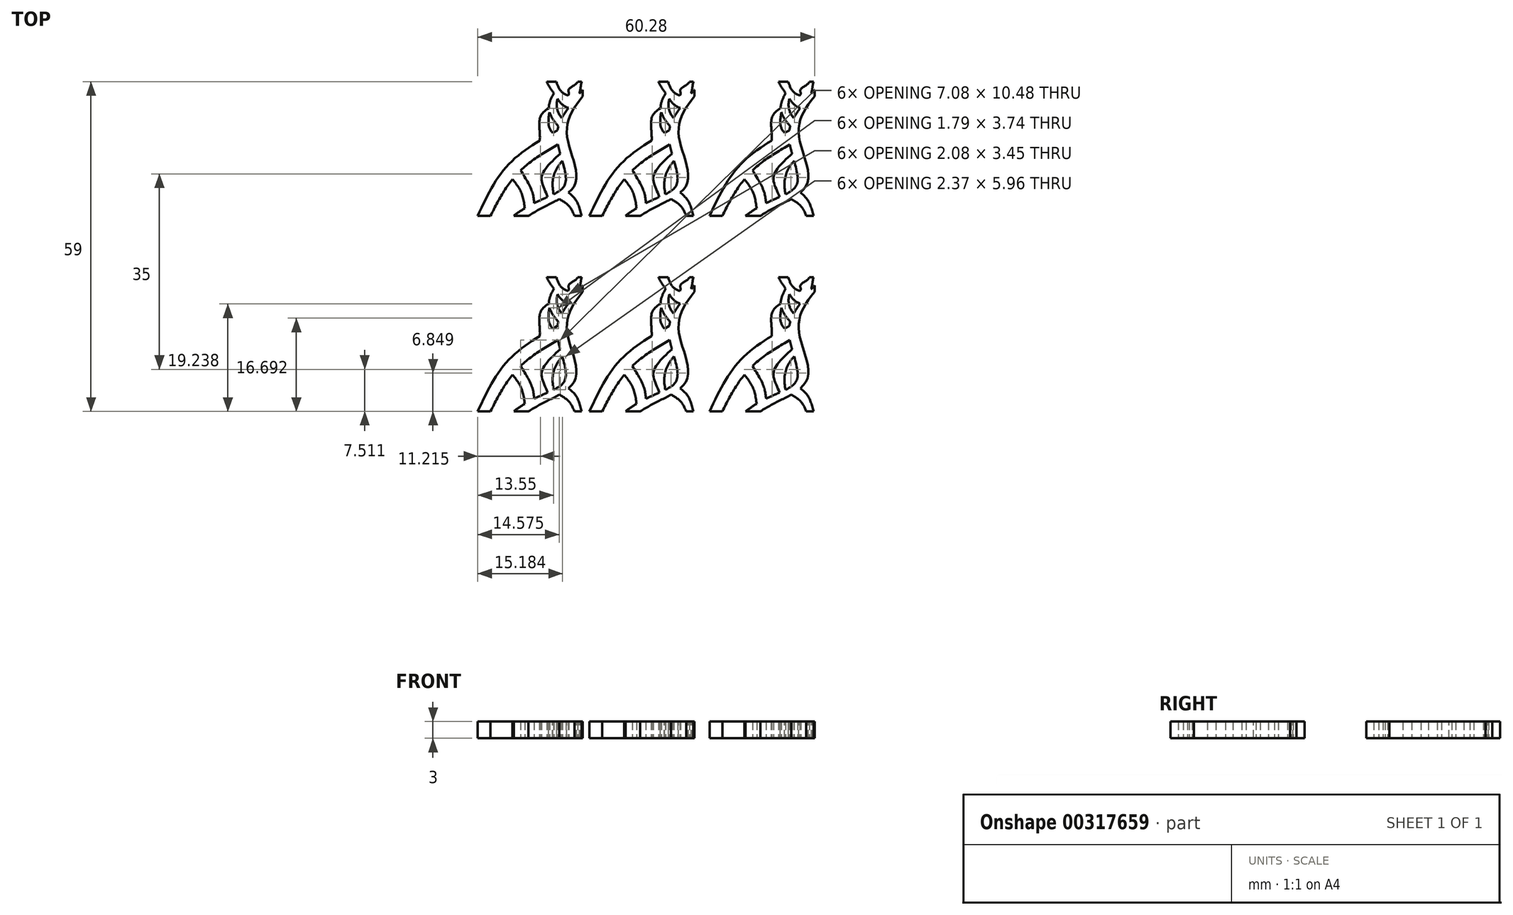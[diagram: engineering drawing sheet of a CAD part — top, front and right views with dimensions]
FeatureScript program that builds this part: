
annotation { "Feature Type Name" : "Feature", "Feature Type Description" : "" }
export const myFeature = defineFeature(function(context is Context, id is Id, definition is map)
    precondition{}
    {
        {
            var Q0;
            Q0=qCreatedBy(makeId("Top.planeOp"),FACE);
            var sketch = newSketch(context, id + "F0", { "sketchPlane" : qUnion([Q0])});
            skLineSegment(sketch, "E0.bottom", {"start": v(161.57, 207.7) * mm, "end": v(-151.57, 207.7) * mm});
            skLineSegment(sketch, "E0.top", {"start": v(161.57, -192.3) * mm, "end": v(-151.57, -192.3) * mm});
            skLineSegment(sketch, "E0.left", {"start": v(161.57, 207.7) * mm, "end": v(161.57, -192.3) * mm});
            skLineSegment(sketch, "E0.right", {"start": v(-151.57, 207.7) * mm, "end": v(-151.57, -192.3) * mm});
            skFitSpline(sketch, "E1", {"points": [v(161.57, 183.5) * mm, v(85.12, 44.75) * mm, v(109.31, -96.4) * mm, v(-44.12, -192.3) * mm], "startDerivative": vector(-382, -492.17) * mm, "endDerivative": vector(-632.26, -490) * mm});
            skFitSpline(sketch, "E2", {"points": [v(161.57, 164.23) * mm, v(115.12, 45.06) * mm, v(139.33, -96.46) * mm, v(0, -192.3) * mm], "startDerivative": vector(-323.93, -389.82) * mm, "endDerivative": vector(-432.8, -289.86) * mm});
            skFitSpline(sketch, "E3", {"points": [v(87.95, 20.15) * mm, v(-36.08, -69.46) * mm, v(-113.36, -192.3) * mm], "startDerivative": vector(-287.2, -159.14) * mm, "endDerivative": vector(-134.26, -271.05) * mm});
            skFitSpline(sketch, "E4", {"points": [v(86.4, 62.77) * mm, v(-60.96, -40.6) * mm, v(-151.57, -192.3) * mm], "startDerivative": vector(-322.1, -181.09) * mm, "endDerivative": vector(-154.33, -329.73) * mm});
            skFitSpline(sketch, "E5", {"points": [v(91.66, -142.16) * mm, v(120.33, -162.57) * mm, v(137.1, -192.3) * mm], "startDerivative": vector(63.12, -36.39) * mm, "endDerivative": vector(28.09, -64.9) * mm});
            skFitSpline(sketch, "E6", {"points": [v(119.32, -123.08) * mm, v(142.68, -147.67) * mm, v(158.5, -192.3) * mm], "startDerivative": vector(55.7, -46.78) * mm, "endDerivative": vector(23.32, -90.23) * mm});
            skFitSpline(sketch, "E7", {"points": [v(100.65, -28.51) * mm, v(73.78, -78.77) * mm, v(75.03, -127.85) * mm], "startDerivative": vector(-88.91, -98.41) * mm, "endDerivative": vector(24.95, -113.83) * mm});
            skFitSpline(sketch, "E8", {"points": [v(94.41, -6.72) * mm, v(39.45, -75.98) * mm, v(57.07, -136.12) * mm], "startDerivative": vector(-135.48, -128.88) * mm, "endDerivative": vector(50.2, -141.27) * mm});
            skFitSpline(sketch, "E9", {"points": [v(54.23, 207.7) * mm, v(81.23, 165.16) * mm, v(119.4, 129.17) * mm], "startDerivative": vector(44.56, -99.42) * mm, "endDerivative": vector(118.17, -31.75) * mm});
            skFitSpline(sketch, "E10", {"points": [v(83.1, 207.7) * mm, v(99.85, 176.33) * mm, v(142.84, 159.86) * mm], "startDerivative": vector(25.78, -76.02) * mm, "endDerivative": vector(99.84, -29.98) * mm});
            skFitSpline(sketch, "E11", {"points": [v(146.4, 207.7) * mm, v(119.4, 183.78) * mm, v(118, 167.02) * mm], "startDerivative": vector(-16.59, -50.41) * mm, "endDerivative": vector(-40.58, -34) * mm});
            skFitSpline(sketch, "E12", {"points": [v(158.5, 207.7) * mm, v(153.85, 181.92) * mm, v(152.97, 172.55) * mm], "startDerivative": vector(-12.64, -48.27) * mm, "endDerivative": vector(10.98, -30.7) * mm});
            skFitSpline(sketch, "E13", {"points": [v(75.43, 173.52) * mm, v(60.75, 128.85) * mm, v(89.2, 75) * mm], "startDerivative": vector(-54.24, -96.72) * mm, "endDerivative": vector(96.14, -103.87) * mm});
            skFitSpline(sketch, "E14", {"points": [v(86.56, 157.05) * mm, v(84.95, 128.85) * mm, v(99.53, 99.55) * mm], "startDerivative": vector(-16.02, -62.32) * mm, "endDerivative": vector(51.54, -60.1) * mm});
            skFitSpline(sketch, "E15", {"points": [v(62.75, 117) * mm, v(60.75, 74.85) * mm, v(72.13, 54.72) * mm], "startDerivative": vector(-16.42, -83.23) * mm, "endDerivative": vector(39.32, -49.75) * mm});
            skFitSpline(sketch, "E16", {"points": [v(60.75, 128.85) * mm, v(35.6, 103.71) * mm, v(32.47, 71.12) * mm, v(33.8, 32.44) * mm], "startDerivative": vector(-112.87, -59.98) * mm, "endDerivative": vector(-6.89, -98.92) * mm});
            skFitSpline(sketch, "E17", {"points": [v(-47.68, -82.88) * mm, v(-21.54, -123.28) * mm, v(-11.06, -169.71) * mm], "startDerivative": vector(59.74, -77.34) * mm, "endDerivative": vector(13.37, -96.33) * mm});
            skFitSpline(sketch, "E18", {"points": [v(-23.58, -56.72) * mm, v(10.06, -118.02) * mm, v(16.93, -154.44) * mm], "startDerivative": vector(70.14, -111.5) * mm, "endDerivative": vector(7.52, -82.35) * mm});
            skSolve(sketch);
        }
        {
            var Q0;
            {var subQ0=sQuery(id+"F0.wireOp",EDGE,"E3");var subQ3=sQuery(id+"F0.wireOp",EDGE,"E1");var subQ4=makeQuery(id+"F0.imprint","INTERSECT",VERTEX,{"derivedFrom":[subQ3,subQ0]});Q0=makeQuery(id+"F0.imprint","IMPRINT",FACE,{"disambiguationData":[TD([[makeQuery(id+"F0.imprint","IMPRINT",EDGE,{"disambiguationData":[TD([[subQ4,1.0]])],"derivedFrom":subQ3}),-1.0]])]});}
            var Q1;
            {var subQ0=sQuery(id+"F0.wireOp",EDGE,"E17");Q1=makeQuery(id+"F0.imprint","IMPRINT",FACE,{"disambiguationData":[TD([[makeQuery(id+"F0.imprint","IMPRINT",EDGE,{"derivedFrom":subQ0}),1.0]])]});}
            var Q2;
            {var subQ0=sQuery(id+"F0.wireOp",EDGE,"E1");var subQ9=sQuery(id+"F0.wireOp",EDGE,"E0.top");var subQ10=makeQuery(id+"F0.imprint","INTERSECT",VERTEX,{"derivedFrom":[subQ9,subQ0]});Q2=makeQuery(id+"F0.imprint","IMPRINT",FACE,{"disambiguationData":[TD([[makeQuery(id+"F0.imprint","IMPRINT",EDGE,{"disambiguationData":[TD([[subQ10,1.0]])],"derivedFrom":subQ9}),-1.0]])]});}
            var Q3;
            {var subQ0=sQuery(id+"F0.wireOp",EDGE,"E5");Q3=makeQuery(id+"F0.imprint","IMPRINT",FACE,{"disambiguationData":[TD([[makeQuery(id+"F0.imprint","IMPRINT",EDGE,{"derivedFrom":subQ0}),1.0]])]});}
            var Q4;
            {var subQ0=sQuery(id+"F0.wireOp",EDGE,"E7");Q4=makeQuery(id+"F0.imprint","IMPRINT",FACE,{"disambiguationData":[TD([[makeQuery(id+"F0.imprint","IMPRINT",EDGE,{"derivedFrom":subQ0}),-1.0]])]});}
            var Q5;
            {var subQ0=sQuery(id+"F0.wireOp",EDGE,"E15");Q5=makeQuery(id+"F0.imprint","IMPRINT",FACE,{"disambiguationData":[TD([[makeQuery(id+"F0.imprint","IMPRINT",EDGE,{"derivedFrom":subQ0}),-1.0]])]});}
            var Q6;
            {var subQ5=sQuery(id+"F0.wireOp",EDGE,"E14");Q6=makeQuery(id+"F0.imprint","IMPRINT",FACE,{"disambiguationData":[TD([[makeQuery(id+"F0.imprint","IMPRINT",EDGE,{"derivedFrom":subQ5}),-1.0]])]});}
            var Q7;
            {var subQ0=sQuery(id+"F0.wireOp",EDGE,"E9");var subQ1=sQuery(id+"F0.wireOp",EDGE,"E0.bottom");var subQ2=makeQuery(id+"F0.imprint","INTERSECT",VERTEX,{"derivedFrom":[subQ1,subQ0]});Q7=makeQuery(id+"F0.imprint","IMPRINT",FACE,{"disambiguationData":[TD([[makeQuery(id+"F0.imprint","IMPRINT",EDGE,{"disambiguationData":[TD([[subQ2,1.0]])],"derivedFrom":subQ1}),1.0]])]});}
            var Q8;
            {var subQ0=sQuery(id+"F0.wireOp",EDGE,"E11");Q8=makeQuery(id+"F0.imprint","IMPRINT",FACE,{"disambiguationData":[TD([[makeQuery(id+"F0.imprint","IMPRINT",EDGE,{"derivedFrom":subQ0}),1.0]])]});}
            extrude(context, id + "F1", {"entities" : qUnion([Q0, Q1, Q2, Q3, Q4, Q5, Q6, Q7, Q8]), "depth" : 50 * mm});
        }
        {
            var Q0;
            Q0=makeQuery(id+"F1.opExtrude","SWEPT_BODY",BODY,{"disambiguationData":[OSD([sQuery(id+"F0.wireOp",EDGE,"E0.bottom"),sQuery(id+"F0.wireOp",EDGE,"E0.top"),sQuery(id+"F0.wireOp",EDGE,"E0.left"),sQuery(id+"F0.wireOp",EDGE,"E1"),sQuery(id+"F0.wireOp",EDGE,"E2"),sQuery(id+"F0.wireOp",EDGE,"E3"),sQuery(id+"F0.wireOp",EDGE,"E4"),sQuery(id+"F0.wireOp",EDGE,"E5"),sQuery(id+"F0.wireOp",EDGE,"E6"),sQuery(id+"F0.wireOp",EDGE,"E7"),sQuery(id+"F0.wireOp",EDGE,"E8"),sQuery(id+"F0.wireOp",EDGE,"E9"),sQuery(id+"F0.wireOp",EDGE,"E10"),sQuery(id+"F0.wireOp",EDGE,"E11"),sQuery(id+"F0.wireOp",EDGE,"E12"),sQuery(id+"F0.wireOp",EDGE,"E13"),sQuery(id+"F0.wireOp",EDGE,"E14"),sQuery(id+"F0.wireOp",EDGE,"E15"),sQuery(id+"F0.wireOp",EDGE,"E16"),sQuery(id+"F0.wireOp",EDGE,"E17"),sQuery(id+"F0.wireOp",EDGE,"E18")])]});
            var Q1;
            Q1=qCreatedBy(makeId("Origin.pointOp"),VERTEX);
            var Q2;
            Q2=qCreatedBy(makeId("Origin.pointOp"),VERTEX);
            transform(context, id + "F2", {"entities" : qUnion([Q0]), "transformType" : TransformType.SCALE_UNIFORMLY, "scale" : 0.06, "scalePoint" : qUnion([Q2]), "makeCopy" : false});
        }
        {
            var Q0;
            Q0=makeQuery(id+"F1.opExtrude","SWEPT_BODY",BODY,{"disambiguationData":[OSD([sQuery(id+"F0.wireOp",EDGE,"E0.bottom"),sQuery(id+"F0.wireOp",EDGE,"E0.top"),sQuery(id+"F0.wireOp",EDGE,"E0.left"),sQuery(id+"F0.wireOp",EDGE,"E1"),sQuery(id+"F0.wireOp",EDGE,"E2"),sQuery(id+"F0.wireOp",EDGE,"E3"),sQuery(id+"F0.wireOp",EDGE,"E4"),sQuery(id+"F0.wireOp",EDGE,"E5"),sQuery(id+"F0.wireOp",EDGE,"E6"),sQuery(id+"F0.wireOp",EDGE,"E7"),sQuery(id+"F0.wireOp",EDGE,"E8"),sQuery(id+"F0.wireOp",EDGE,"E9"),sQuery(id+"F0.wireOp",EDGE,"E10"),sQuery(id+"F0.wireOp",EDGE,"E11"),sQuery(id+"F0.wireOp",EDGE,"E12"),sQuery(id+"F0.wireOp",EDGE,"E13"),sQuery(id+"F0.wireOp",EDGE,"E14"),sQuery(id+"F0.wireOp",EDGE,"E15"),sQuery(id+"F0.wireOp",EDGE,"E16"),sQuery(id+"F0.wireOp",EDGE,"E17"),sQuery(id+"F0.wireOp",EDGE,"E18")])]});
            transform(context, id + "F3", {"entities" : qUnion([Q0]), "transformType" : TransformType.TRANSLATION_3D, "dx" : 21.5 * mm, "dy" : 0 * mm, "dz" : 0 * mm, "makeCopy" : true});
        }
        {
            var Q0;
            Q0=makeQuery(id+"F1.opExtrude","SWEPT_BODY",BODY,{"disambiguationData":[OSD([sQuery(id+"F0.wireOp",EDGE,"E0.bottom"),sQuery(id+"F0.wireOp",EDGE,"E0.top"),sQuery(id+"F0.wireOp",EDGE,"E0.left"),sQuery(id+"F0.wireOp",EDGE,"E1"),sQuery(id+"F0.wireOp",EDGE,"E2"),sQuery(id+"F0.wireOp",EDGE,"E3"),sQuery(id+"F0.wireOp",EDGE,"E4"),sQuery(id+"F0.wireOp",EDGE,"E5"),sQuery(id+"F0.wireOp",EDGE,"E6"),sQuery(id+"F0.wireOp",EDGE,"E7"),sQuery(id+"F0.wireOp",EDGE,"E8"),sQuery(id+"F0.wireOp",EDGE,"E9"),sQuery(id+"F0.wireOp",EDGE,"E10"),sQuery(id+"F0.wireOp",EDGE,"E11"),sQuery(id+"F0.wireOp",EDGE,"E12"),sQuery(id+"F0.wireOp",EDGE,"E13"),sQuery(id+"F0.wireOp",EDGE,"E14"),sQuery(id+"F0.wireOp",EDGE,"E15"),sQuery(id+"F0.wireOp",EDGE,"E16"),sQuery(id+"F0.wireOp",EDGE,"E17"),sQuery(id+"F0.wireOp",EDGE,"E18")])]});
            transform(context, id + "F4", {"entities" : qUnion([Q0]), "transformType" : TransformType.TRANSLATION_3D, "dx" : -20 * mm, "dy" : 0 * mm, "dz" : 0 * mm, "makeCopy" : true});
        }
        {
            var Q0;
            Q0=makeQuery(id+"F1.opExtrude","SWEPT_BODY",BODY,{"disambiguationData":[OSD([sQuery(id+"F0.wireOp",EDGE,"E0.bottom"),sQuery(id+"F0.wireOp",EDGE,"E0.top"),sQuery(id+"F0.wireOp",EDGE,"E0.left"),sQuery(id+"F0.wireOp",EDGE,"E1"),sQuery(id+"F0.wireOp",EDGE,"E2"),sQuery(id+"F0.wireOp",EDGE,"E3"),sQuery(id+"F0.wireOp",EDGE,"E4"),sQuery(id+"F0.wireOp",EDGE,"E5"),sQuery(id+"F0.wireOp",EDGE,"E6"),sQuery(id+"F0.wireOp",EDGE,"E7"),sQuery(id+"F0.wireOp",EDGE,"E8"),sQuery(id+"F0.wireOp",EDGE,"E9"),sQuery(id+"F0.wireOp",EDGE,"E10"),sQuery(id+"F0.wireOp",EDGE,"E11"),sQuery(id+"F0.wireOp",EDGE,"E12"),sQuery(id+"F0.wireOp",EDGE,"E13"),sQuery(id+"F0.wireOp",EDGE,"E14"),sQuery(id+"F0.wireOp",EDGE,"E15"),sQuery(id+"F0.wireOp",EDGE,"E16"),sQuery(id+"F0.wireOp",EDGE,"E17"),sQuery(id+"F0.wireOp",EDGE,"E18")])]});
            transform(context, id + "F5", {"entities" : qUnion([Q0]), "transformType" : TransformType.TRANSLATION_3D, "dx" : 0 * mm, "dy" : 35 * mm, "dz" : 0 * mm, "makeCopy" : true});
        }
        {
            var Q0;
            Q0=makeQuery(id+"F3.opPattern","COPY",BODY,{"derivedFrom":makeQuery(id+"F1.opExtrude","SWEPT_BODY",BODY,{"disambiguationData":[OSD([sQuery(id+"F0.wireOp",EDGE,"E0.bottom"),sQuery(id+"F0.wireOp",EDGE,"E0.top"),sQuery(id+"F0.wireOp",EDGE,"E0.left"),sQuery(id+"F0.wireOp",EDGE,"E1"),sQuery(id+"F0.wireOp",EDGE,"E2"),sQuery(id+"F0.wireOp",EDGE,"E3"),sQuery(id+"F0.wireOp",EDGE,"E4"),sQuery(id+"F0.wireOp",EDGE,"E5"),sQuery(id+"F0.wireOp",EDGE,"E6"),sQuery(id+"F0.wireOp",EDGE,"E7"),sQuery(id+"F0.wireOp",EDGE,"E8"),sQuery(id+"F0.wireOp",EDGE,"E9"),sQuery(id+"F0.wireOp",EDGE,"E10"),sQuery(id+"F0.wireOp",EDGE,"E11"),sQuery(id+"F0.wireOp",EDGE,"E12"),sQuery(id+"F0.wireOp",EDGE,"E13"),sQuery(id+"F0.wireOp",EDGE,"E14"),sQuery(id+"F0.wireOp",EDGE,"E15"),sQuery(id+"F0.wireOp",EDGE,"E16"),sQuery(id+"F0.wireOp",EDGE,"E17"),sQuery(id+"F0.wireOp",EDGE,"E18")])]}),"instanceName":"1"});
            transform(context, id + "F6", {"entities" : qUnion([Q0]), "transformType" : TransformType.TRANSLATION_3D, "dx" : 0 * mm, "dy" : 35 * mm, "dz" : 0 * mm, "makeCopy" : true});
        }
        {
            var Q0;
            Q0=makeQuery(id+"F4.opPattern","COPY",BODY,{"derivedFrom":makeQuery(id+"F1.opExtrude","SWEPT_BODY",BODY,{"disambiguationData":[OSD([sQuery(id+"F0.wireOp",EDGE,"E0.bottom"),sQuery(id+"F0.wireOp",EDGE,"E0.top"),sQuery(id+"F0.wireOp",EDGE,"E0.left"),sQuery(id+"F0.wireOp",EDGE,"E1"),sQuery(id+"F0.wireOp",EDGE,"E2"),sQuery(id+"F0.wireOp",EDGE,"E3"),sQuery(id+"F0.wireOp",EDGE,"E4"),sQuery(id+"F0.wireOp",EDGE,"E5"),sQuery(id+"F0.wireOp",EDGE,"E6"),sQuery(id+"F0.wireOp",EDGE,"E7"),sQuery(id+"F0.wireOp",EDGE,"E8"),sQuery(id+"F0.wireOp",EDGE,"E9"),sQuery(id+"F0.wireOp",EDGE,"E10"),sQuery(id+"F0.wireOp",EDGE,"E11"),sQuery(id+"F0.wireOp",EDGE,"E12"),sQuery(id+"F0.wireOp",EDGE,"E13"),sQuery(id+"F0.wireOp",EDGE,"E14"),sQuery(id+"F0.wireOp",EDGE,"E15"),sQuery(id+"F0.wireOp",EDGE,"E16"),sQuery(id+"F0.wireOp",EDGE,"E17"),sQuery(id+"F0.wireOp",EDGE,"E18")])]}),"instanceName":"1"});
            transform(context, id + "F7", {"entities" : qUnion([Q0]), "transformType" : TransformType.TRANSLATION_3D, "dx" : 0 * mm, "dy" : 35 * mm, "dz" : 0 * mm, "makeCopy" : true});
        }
    });
